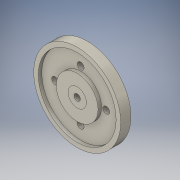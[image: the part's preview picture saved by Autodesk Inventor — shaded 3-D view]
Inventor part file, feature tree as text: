
AUTODESK INVENTOR PART (.ipt)
format: ipt  version: 2016 (Build 200138000, 138)  size: 285,696 bytes
history: native  units: in
note: dims shown in document units (in); Inventor stores cm internally (conversion verified against a paired STEP export)
features: extrude x7, sketch x7, plane x1
ambient origin geometry x8: Origin, YZ Plane, XZ Plane, XY Plane, X Axis, Y Axis, Z Axis, Center Point
bodies: Solid1 (feature_tree)
feature tree (15):
  extrude  "Extrusion1"  Depth=0.2in TaperAngle=0.0deg
  extrude  "Extrusion2"  Depth=1.52in
  extrude  "Extrusion3"  Depth=0.36in
  extrude  "Extrusion5"  Depth=0.5in TaperAngle=0.0deg
  extrude  "Extrusion6"  Depth=0.18in TaperAngle=0.0deg
  extrude  "Extrusion8"  Depth=0.133in
  plane  "Work Plane1"
  extrude  "Extrusion9"  Depth=0.5in
  sketch  "Sketch1"  dims[d0=1.7in d1=0.2in d2=0.0in]
  sketch  "Sketch2"  dims[d3=0.816in d4=1.52in]
  sketch  "Sketch3"  dims[d5=0.068in d6=0.0in d7=0.36in]
  sketch  "Sketch5"  dims[d8=0.0001in d9=0.5in d10=0.0in d11=0.0in d17=0.45in d18=0.0in]
  sketch  "Sketch6"  dims[d19=0.125in d20=0.18in d21=0.0in]
  sketch  "Sketch8"  dims[d25=0.133in d26=0.133in]
  sketch  "Sketch9"  dims[d29=0.133in d30=0.133in d33=1.0in d34=0.0in d35=0.1in d36=1.0in d37=0.0in d38=0.5in d39=0.5in d40=0.5in d41=0.5in]
